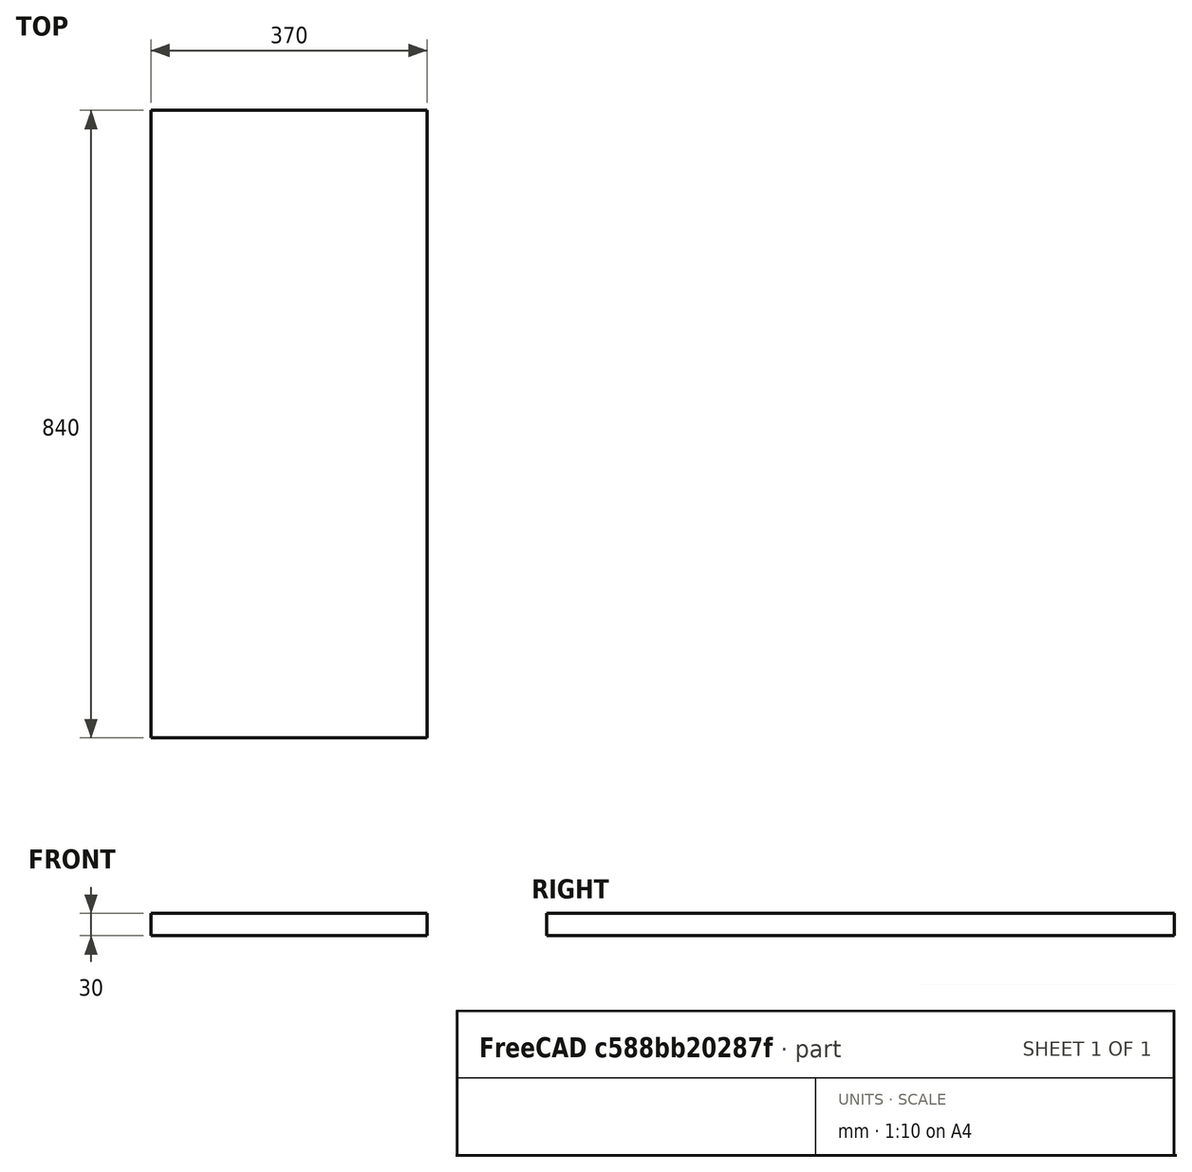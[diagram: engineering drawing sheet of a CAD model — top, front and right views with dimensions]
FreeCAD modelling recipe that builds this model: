
FCSTD DOCUMENT  (FreeCAD 0.20R29603 (Git))
Label: UnterbodenHinten
License: All rights reserved
LicenseURL: http://en.wikipedia.org/wiki/All_rights_reserved
objects: Sketcher::SketchObject×1, PartDesign::Pad×1, PartDesign::Body×1
note: 4 computed .brp shape members not serialized (recipe doc carries the construction recipe); baked Part::Feature solids carry a one-line shape summary decoded from their .brp

FEATURE [Sketcher::SketchObject] Sketch
  FullyConstrained = true
  MapMode = 5
  Support = -> [XY_Plane]
  sketch-geometry (5):
    g0: LineSegment StartX=-185 StartY=420 StartZ=0 EndX=-185 EndY=-420 EndZ=0
    g1: LineSegment StartX=-185 StartY=-420 StartZ=0 EndX=185 EndY=-420 EndZ=0
    g2: LineSegment StartX=185 StartY=-420 StartZ=0 EndX=185 EndY=420 EndZ=0
    g3: LineSegment StartX=185 StartY=420 StartZ=0 EndX=-185 EndY=420 EndZ=0
    g4: GeomPoint X=0 Y=0 Z=0
  constraints (12):
    c: Coincident(g0,g1)
    c: Coincident(g1,g2)
    c: Coincident(g2,g3)
    c: Coincident(g3,g0)
    c: Horizontal(g1)
    c: Horizontal(g3)
    c: Vertical(g0)
    c: Vertical(g2)
    c: Symmetric(g1,g0,g4)
    c: Coincident(g4,g-1)
    c: Distance(g2) = 840
    c: Distance(g1) = 370
FEATURE [PartDesign::Pad] Pad
  Direction = (0,0,1)
  Length = 30
  Length2 = 10
  Profile = -> Sketch
  ReferenceAxis = -> Sketch [N_Axis]
  Type = 0
FEATURE [PartDesign::Body] Body
  Group = -> [Sketch,Pad]
  Origin = -> Origin
  Tip = -> Pad
